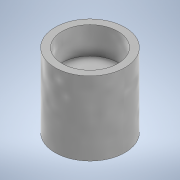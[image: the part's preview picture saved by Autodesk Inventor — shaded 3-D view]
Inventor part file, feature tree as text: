
AUTODESK INVENTOR PART (.ipt)
format: ipt  version: 2022 (Build 260153000, 153)  size: 128,512 bytes
history: native  units: mm
features: sketch x3, extrude x2
ambient origin geometry x8: Origin, YZ Plane, XZ Plane, XY Plane, X Axis, Y Axis, Z Axis, Center Point
bodies: 实体1 (feature_tree)
feature tree (5):
  sketch  "草图1"  dims[d0=9.0mm d1=3.2mm]
  extrude  "拉伸1"  Depth=3.2mm
  extrude  "拉伸2"  Depth=2.5mm
  sketch  "草图2"  dims[d2=2.7mm d3=2.5mm]
  sketch  "草图3"  dims[d4=6.0mm d5=0.0mm d6=7.2mm d7=3.5mm d8=0.0mm]
